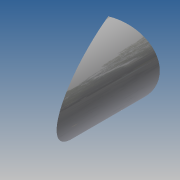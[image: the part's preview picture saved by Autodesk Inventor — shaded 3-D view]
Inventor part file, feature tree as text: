
AUTODESK INVENTOR PART (.ipt)
format: ipt  version: 2017.3 (Build 213257000, 257)  size: 286,208 bytes
history: native  units: in
note: dims shown in document units (in); Inventor stores cm internally (conversion verified against a paired STEP export)
features: extrude x2, other x2, sketch x2, plane x1
ambient origin geometry x8: Origin, YZ Plane, XZ Plane, XY Plane, X Axis, Y Axis, Z Axis, Center Point
bodies: Solid1 (feature_tree)
feature tree (7):
  extrude  "Extrusion1"  Depth=35.25in
  extrude  "Extrusion2"  Depth=70.0in TaperAngle=0.0deg
  other  "A-Side Definition"
  sketch  "Sketch1"  dims[d0=32.25in d1=35.25in]
  sketch  "Sketch2"  dims[d2=50.9606in d3=17.4961in d4=0.0in d5=0.0in d8=70.0in d9=0.0in d10=32.375in d79=22.5deg]
  other  "Definition1"
  plane  "Work Plane1"
